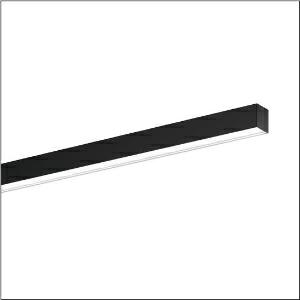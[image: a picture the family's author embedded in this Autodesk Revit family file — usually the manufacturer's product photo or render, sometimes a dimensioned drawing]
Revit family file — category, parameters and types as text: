
# Revit family: silica_r__21_51mx20dc35bb_a1de
name_source: partatom
category: Lighting Fixtures
units: mm (PartAtom-declared; Revit-internal decimal feet)

## family parameters
Cut with Voids When Loaded = No
Host = Face
Light Source = No
Part Type = Normal
Room Calculation Point = No
Round Connector Dimension = Use Diameter
Shared = No

## types (1)
- --- (1 x LED, 6000 lm, 42.6 W, 3000K)
    Apparent Load = 43 VA
    CIE Flux Codes = 48 79 96 100 100
    Color Rendering = 80
    Color Temperature = 3000K
    Default Elevation = 1800 mm
    Description = Silica® 21, office luminaire, primary optical cover: cover, of PMMA, opal, light emission: direct distribution, primary light characteristic: symmetric, installation type: surface-mounted, LED, rated luminous flux: 6.000lm, luminous efficacy: 141lm/W, light colour: 830, colour temperature: 3000K, with terminal, 3+2-pole, max. 2.5mm², mains connection: 220..240V, AC, 50/60Hz, rated input power: 42.6W, luminaire housing, of aluminium, jet black (RAL 9005), length: 3.004mm, width: 53mm, height: 53mm, protection rating (complete): IP20, insulation class (complete): insulation class I (protective earthing), certification: CE, permissible operating ambient temperature: 0..+35°C, standard: EN 50419, packaging unit: 1 piece
    Height = 0 mm  [stored 0 ft]
    Lamp = 1 x LED
    Lamp Light Flux = 6000 lm
    Lamp Power = 42.6 W
    Lamp count = 1
    Length = 3004 mm
    Luminous efficacy = 141 lm/W
    Manufacturer = Siteco
    ModVariant = No
    Model = 51MX20DC35BB
    Mounting Place = Ceiling
    Mounting Type = Recessed
    Number of Poles = 1
    OnlyDefault = Yes
    Power Factor = 1
    Product Name = Silica® 21
    Product group = office luminaire | ceiling recessed
    ProductGroupID = 400
    Protection Class = Protection class I
    Protection Degree = IP 20
    RLX_Detail_Level = 1
    RLX_Emergency_Light_Flux = 0 lm
    RLX_Emergency_Type = 0
    RLX_Emergency_Type_DB = No
    RlxData = <blob elided: 28897 chars, md5=66457153>
    Socket = socket
    Standby Power = 0 W
    System Light Flux = 6000 lm
    System Power = 43 W
    Type Comments = factory setting: luminous flux: 100 % | dim-lin: 254 | 233 mA
    Type Image = l_1335925.jpg
    URL = http://relux.com
    VarID = @adj_086729
    Voltage = 0 V
    Weight = 0.00 kg
    Width = 53 mm

note: [stored X ft] marks values corroborated as IEEE doubles in the binary element streams (Revit-internal decimal feet)

## geometry (parser evidence)
native form markers: Blend x4, Sweep x10
no freeform markers — native parametric forms only
